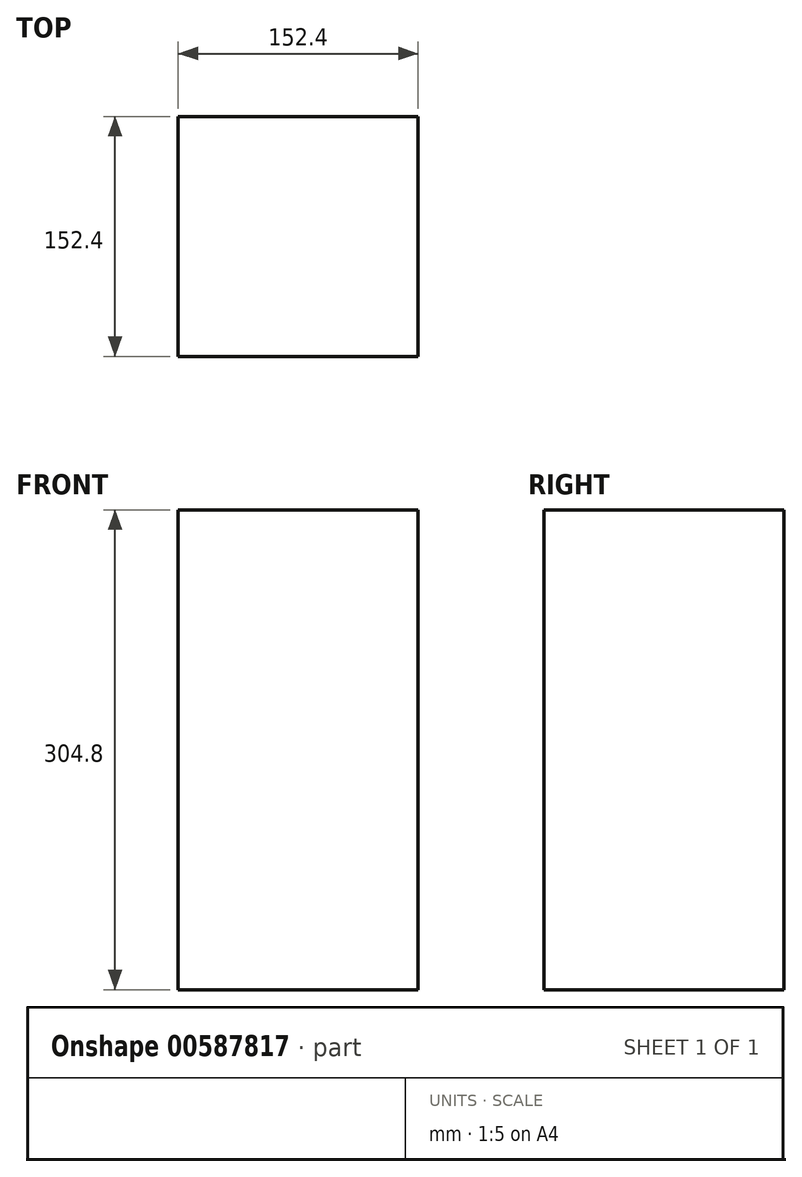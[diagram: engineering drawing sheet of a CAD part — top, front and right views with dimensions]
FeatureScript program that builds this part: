
annotation { "Feature Type Name" : "Feature", "Feature Type Description" : "" }
export const myFeature = defineFeature(function(context is Context, id is Id, definition is map)
    precondition{}
    {
        {
            var Q0;
            Q0=qCreatedBy(makeId("Front.planeOp"),FACE);
            var sketch = newSketch(context, id + "F0", { "sketchPlane" : qUnion([Q0])});
            skLineSegment(sketch, "E0.bottom", {"start": v(-73.47, 234.24) * mm, "end": v(78.93, 234.24) * mm});
            skLineSegment(sketch, "E0.top", {"start": v(-73.47, -70.56) * mm, "end": v(78.93, -70.56) * mm});
            skLineSegment(sketch, "E0.left", {"start": v(-73.47, 234.24) * mm, "end": v(-73.47, -70.56) * mm});
            skLineSegment(sketch, "E0.right", {"start": v(78.93, 234.24) * mm, "end": v(78.93, -70.56) * mm});
            skSolve(sketch);
        }
        {
            var Q0;
            Q0=makeQuery(id+"F0.imprint","IMPRINT",FACE,{"disambiguationData":[TD([[makeQuery(id+"F0.imprint","IMPRINT",EDGE,{"derivedFrom":sQuery(id+"F0.wireOp",EDGE,"E0.bottom")}),-1.0]])]});
            extrude(context, id + "F1", {"entities" : qUnion([Q0]), "depth" : 152.4 * mm, "offsetDistance" : 25.4 * mm});
        }
    });
